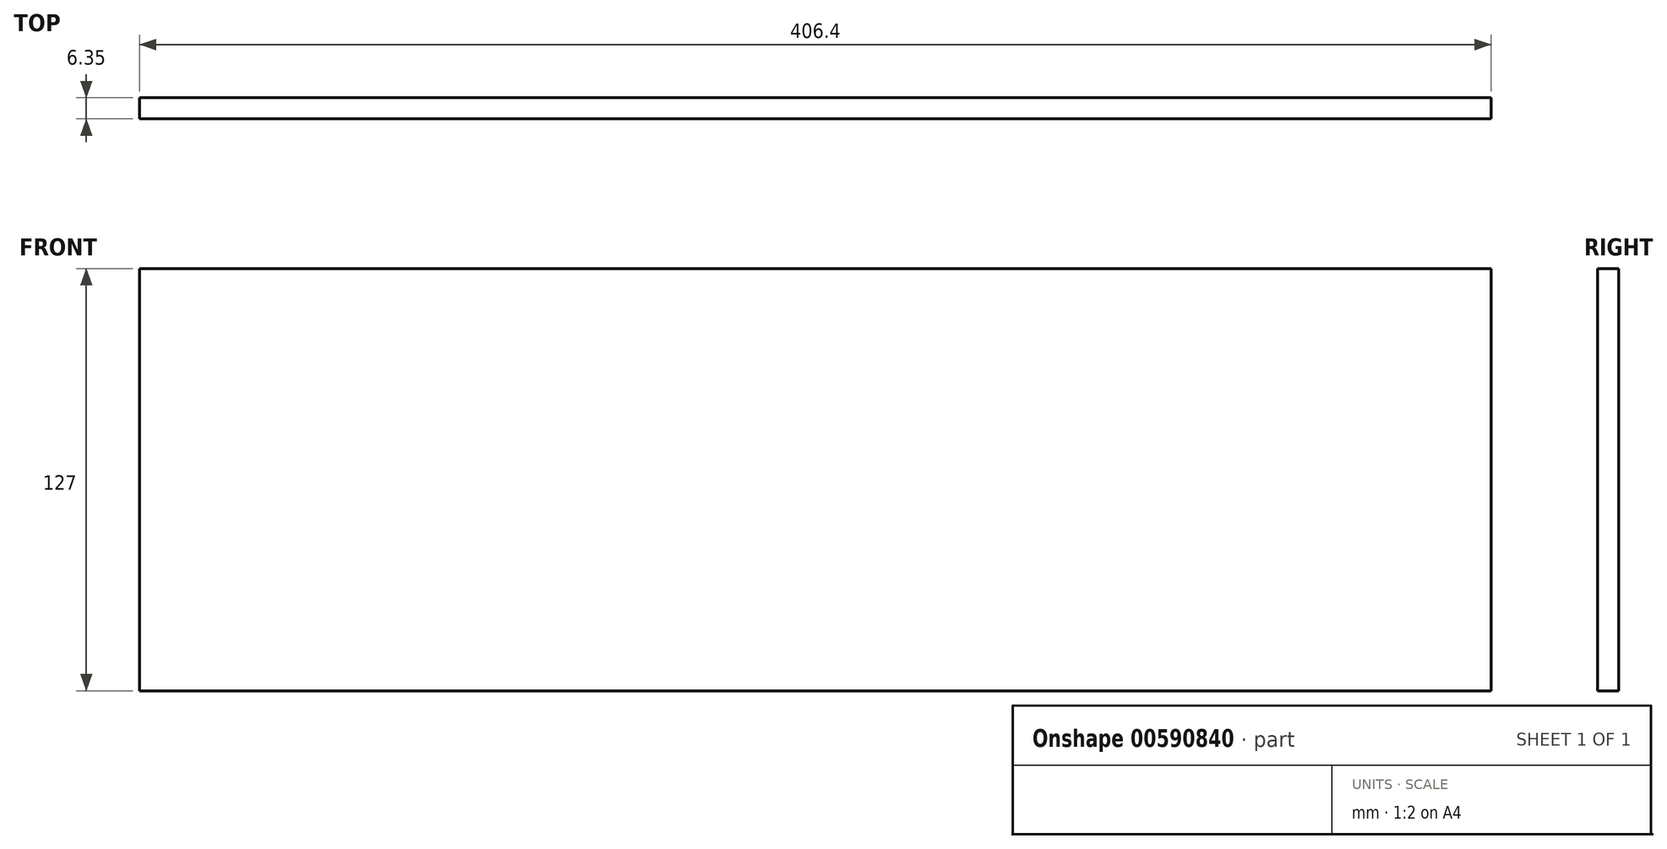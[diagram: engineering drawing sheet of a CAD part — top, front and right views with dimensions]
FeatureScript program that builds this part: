
annotation { "Feature Type Name" : "Feature", "Feature Type Description" : "" }
export const myFeature = defineFeature(function(context is Context, id is Id, definition is map)
    precondition{}
    {
        {
            var Q0;
            Q0=qCreatedBy(makeId("Front.planeOp"),FACE);
            var sketch = newSketch(context, id + "F0", { "sketchPlane" : qUnion([Q0])});
            skLineSegment(sketch, "E0.bottom", {"start": v(173.99, -93.55) * mm, "end": v(-232.41, -93.55) * mm});
            skLineSegment(sketch, "E0.top", {"start": v(173.99, -220.55) * mm, "end": v(-232.41, -220.55) * mm});
            skLineSegment(sketch, "E0.left", {"start": v(173.99, -93.55) * mm, "end": v(173.99, -220.55) * mm});
            skLineSegment(sketch, "E0.right", {"start": v(-232.41, -93.55) * mm, "end": v(-232.41, -220.55) * mm});
            skSolve(sketch);
        }
        {
            var Q0;
            Q0=makeQuery(id+"F0.imprint","IMPRINT",FACE,{"disambiguationData":[TD([[makeQuery(id+"F0.imprint","IMPRINT",EDGE,{"derivedFrom":sQuery(id+"F0.wireOp",EDGE,"E0.bottom")}),1.0]])]});
            extrude(context, id + "F1", {"entities" : qUnion([Q0]), "depth" : 6.35 * mm, "offsetDistance" : 25.4 * mm});
        }
    });
